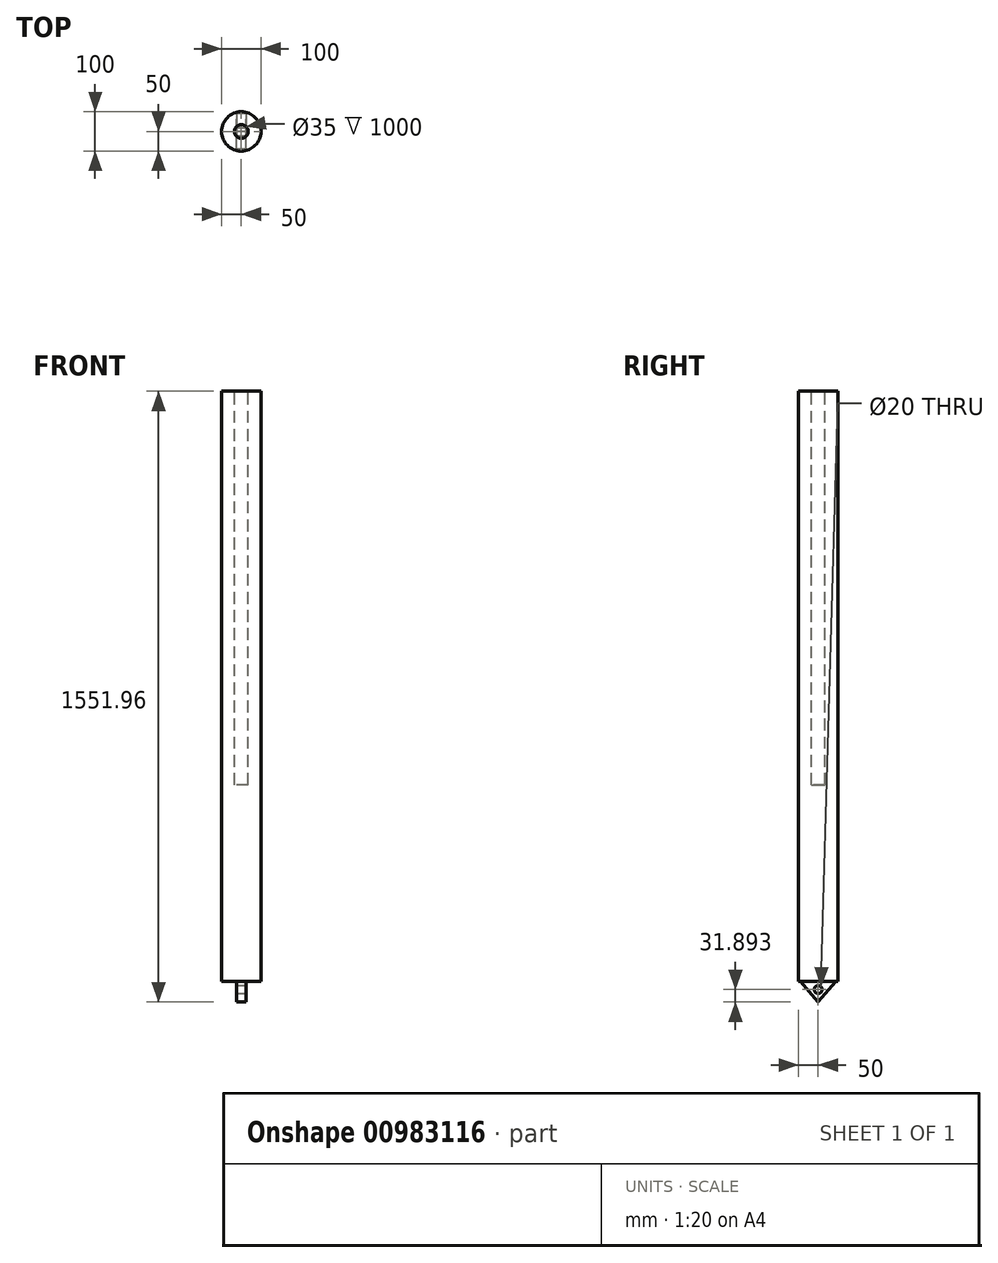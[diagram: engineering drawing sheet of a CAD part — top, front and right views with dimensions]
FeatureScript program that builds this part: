
annotation { "Feature Type Name" : "Feature", "Feature Type Description" : "" }
export const myFeature = defineFeature(function(context is Context, id is Id, definition is map)
    precondition{}
    {
        {
            var Q0;
            Q0=qCreatedBy(makeId("Top.planeOp"),FACE);
            var sketch = newSketch(context, id + "F0", { "sketchPlane" : qUnion([Q0])});
            skCircle(sketch, "E0", {"center": v(0, 0) * mm, "radius": 50 * mm});
            skSolve(sketch);
        }
        {
            var Q0;
            Q0=makeQuery(id+"F0.imprint","IMPRINT",FACE,{"disambiguationData":[TD([[makeQuery(id+"F0.imprint","IMPRINT",EDGE,{"derivedFrom":sQuery(id+"F0.wireOp",EDGE,"E0")}),1.0]])]});
            extrude(context, id + "F1", {"entities" : qUnion([Q0]), "depth" : 1500 * mm, "offsetDistance" : 25 * mm});
        }
        {
            var Q0;
            Q0=makeQuery(id+"F1.opExtrude","CAP_FACE",FACE,{"disambiguationData":[OSD([sQuery(id+"F0.wireOp",EDGE,"E0")])],"isStart":false});
            var sketch = newSketch(context, id + "F2", { "sketchPlane" : qUnion([Q0])});
            skCircle(sketch, "E1", {"center": v(0, 0) * mm, "radius": 17.5 * mm});
            skSolve(sketch);
        }
        {
            var Q0;
            Q0 = qSketchRegion(id + "F2", true);
            extrude(context, id + "F3", {"entities" : qUnion([Q0]), "operationType" : NewBodyOperationType.REMOVE, "oppositeDirection" : true, "depth" : 1000 * mm, "offsetDistance" : 25 * mm});
        }
        {
            var Q0;
            Q0=qCreatedBy(makeId("Right.planeOp"),FACE);
            var sketch = newSketch(context, id + "F4", { "sketchPlane" : qUnion([Q0])});
            skLineSegment(sketch, "E2", {"start": v(-45, 0) * mm, "end": v(0, -51.96) * mm});
            skLineSegment(sketch, "E3.MirrorCS", {"start": v(45, 0) * mm, "end": v(0, -51.96) * mm});
            skLineSegment(sketch, "E4", {"start": v(-45, 0) * mm, "end": v(45, 0) * mm});
            skSolve(sketch);
        }
        {
            var Q0;
            Q0 = qSketchRegion(id + "F4", true);
            extrude(context, id + "F5", {"entities" : qUnion([Q0]), "endBound" : BoundingType.SYMMETRIC, "depth" : 25 * mm, "offsetDistance" : 25 * mm});
        }
        {
            var Q0;
            Q0=qCreatedBy(makeId("Right.planeOp"),FACE);
            var sketch = newSketch(context, id + "F6", { "sketchPlane" : qUnion([Q0])});
            skCircle(sketch, "E5", {"center": v(0, -20.07) * mm, "radius": 10 * mm});
            skSolve(sketch);
        }
        {
            var Q0;
            Q0 = qSketchRegion(id + "F6", true);
            var Q1;
            Q1=makeQuery(id+"F5.opExtrude","CAP_FACE",FACE,{"disambiguationData":[OSD([sQuery(id+"F4.wireOp",EDGE,"E2"),sQuery(id+"F4.wireOp",EDGE,"E3.MirrorCS"),sQuery(id+"F4.wireOp",EDGE,"E4")])],"isStart":true});
            extrude(context, id + "F7", {"entities" : qUnion([Q0]), "operationType" : NewBodyOperationType.REMOVE, "endBound" : BoundingType.SYMMETRIC, "oppositeDirection" : true, "depth" : 25 * mm, "endBoundEntityFace" : qUnion([Q1]), "offsetDistance" : 25 * mm});
        }
    });
